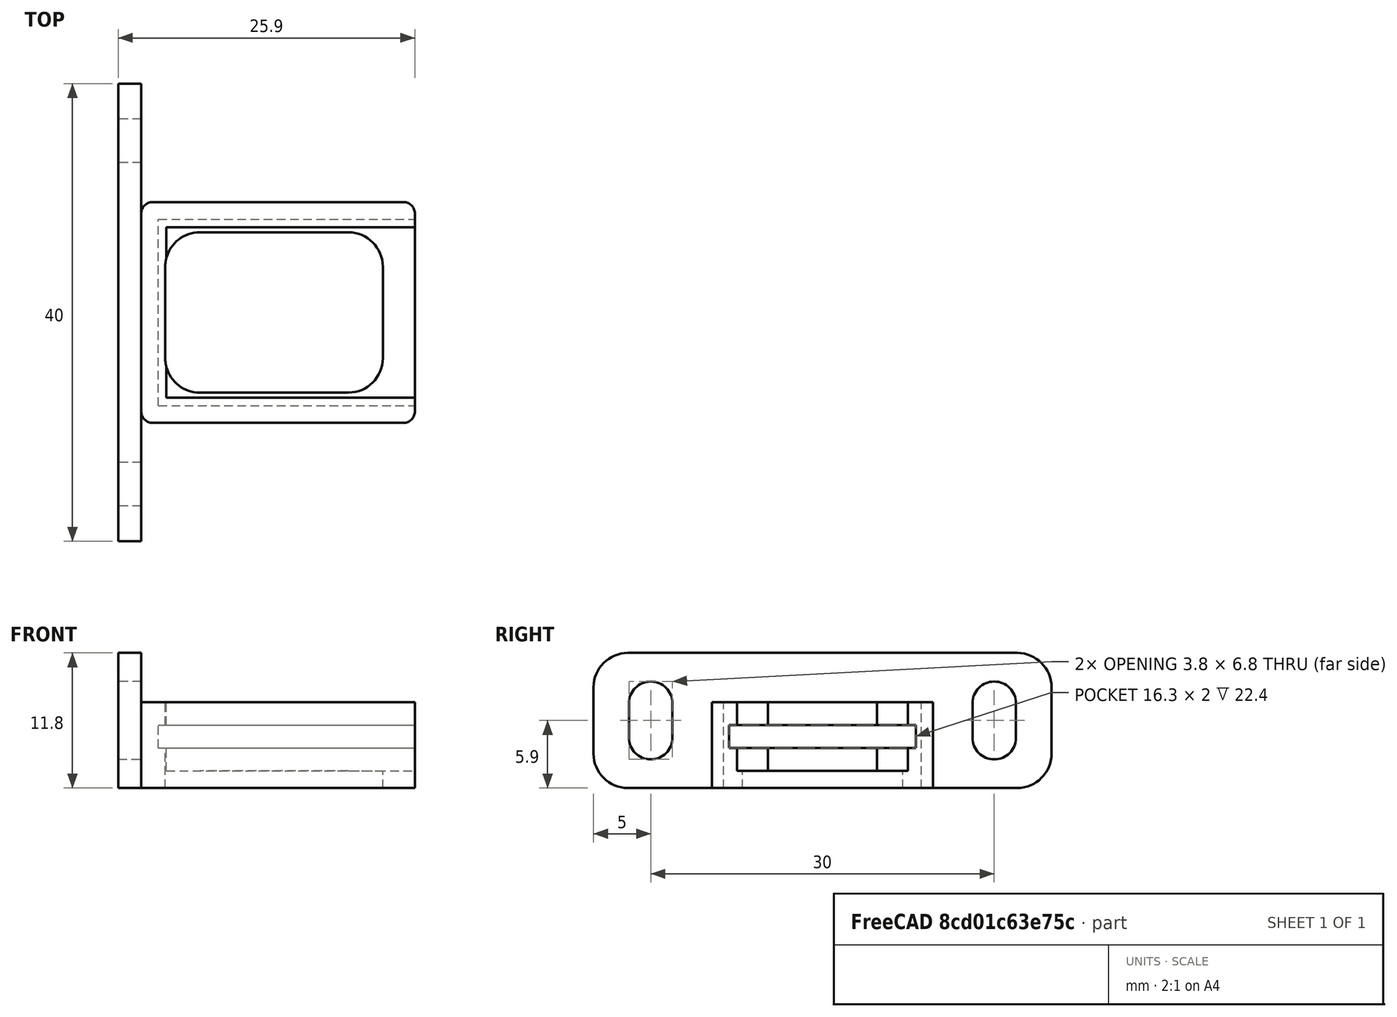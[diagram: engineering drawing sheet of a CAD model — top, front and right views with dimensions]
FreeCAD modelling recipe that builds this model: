
FCSTD DOCUMENT  (FreeCAD 0.21R33694 (Git))
Label: hlk-ld2410c
License: FreeArt
LicenseURL: http://artlibre.org/licence/lal
objects: Part::Box×4, Part::Fillet×2, Part::MultiFuse×2, Spreadsheet::Sheet×1, Part::Feature×1, Part::Cut×1, App::Part×1
note: 10 computed .brp shape members not serialized (recipe doc carries the construction recipe); baked Part::Feature solids carry a one-line shape summary decoded from their .brp

FEATURE [Spreadsheet::Sheet] Spreadsheet  label="p"
  cells = A1='pcb_x; B1(pcb_x)=22.4; A2='pcb_y; B2(pcb_y)=16.3; A3='pcb_z; B3(pcb_z)=2; A4='pcb_under; B4(pcb_under)=2; A5='side_wall; B5(side_wall)=1.5; A6='pcb_side_lane; B6(pcb_side_lane)=0.7; A7='bottom_wall; B7(bottom_wall)=1.5; A8='pcb_above; B8(pcb_above)=2; A9='bottom_hole_x; B9(bottom_hole_x)=19; A10='bottom_hole_y; B10(bottom_hole_y)=14
FEATURE [Part::Box] Box  label="external cube"
  AttacherType = Attacher::AttachEngine3D
  Height = 7.5
  Length = 23.9
  Width = 19.3
  expr: Height = <<p>>.bottom_wall + <<p>>.pcb_under + <<p>>.pcb_z + <<p>>.pcb_above
  expr: Length = <<p>>.pcb_x + <<p>>.side_wall
  expr: Width = <<p>>.pcb_y + 2 * <<p>>.side_wall
FEATURE [Part::Box] Box006  label="internal cube"
  AttacherType = Attacher::AttachEngine3D
  Height = 6
  Length = 22.5
  Placement = pos=(2.2,2.2,1.5) rot=(0,0,1;0rad)
  Width = 14.9
  expr: .Placement.Base.x = <<p>>.side_wall + <<p>>.pcb_side_lane
  expr: .Placement.Base.y = <<p>>.side_wall + <<p>>.pcb_side_lane
  expr: .Placement.Base.z = <<p>>.bottom_wall
  expr: Height = <<p>>.pcb_under + <<p>>.pcb_z + <<p>>.pcb_above
  expr: Length = <<p>>.pcb_x - 2 * <<p>>.pcb_side_lane + <<p>>.side_wall
  expr: Width = <<p>>.pcb_y - 2 * <<p>>.pcb_side_lane
FEATURE [Part::Box] Box007  label="pcb extract cube"
  AttacherType = Attacher::AttachEngine3D
  Height = 2
  Length = 22.4
  Placement = pos=(1.5,1.5,3.5) rot=(0,0,1;0rad)
  Width = 16.3
  expr: .Placement.Base.x = <<p>>.side_wall
  expr: .Placement.Base.y = <<p>>.side_wall
  expr: .Placement.Base.z = <<p>>.bottom_wall + <<p>>.pcb_under
  expr: Height = <<p>>.pcb_z
  expr: Length = <<p>>.pcb_x
  expr: Width = <<p>>.pcb_y
FEATURE [Part::Fillet] Fillet  label="external fillet"
  Base = -> Box
  Edges = 4 edges r=1: [Edge1,Edge3,Edge5,Edge7]
FEATURE [Part::Box] Box008  label="bottom hole"
  AttacherType = Attacher::AttachEngine3D
  Height = 10
  Length = 19
  Placement = pos=(2.1,2.65,0) rot=(0,0,1;0rad)
  Width = 14
  expr: .Placement.Base.x = (<<p>>.pcb_x + <<p>>.side_wall - <<p>>.pcb_side_lane - <<p>>.bottom_hole_x) / 2
  expr: .Placement.Base.y = (<<p>>.pcb_y + 2 * <<p>>.side_wall - <<p>>.bottom_hole_y) / 2
  expr: Length = <<p>>.bottom_hole_x
  expr: Width = <<p>>.bottom_hole_y
FEATURE [Part::Fillet] Fillet001  label="bottom hole fillet"
  Base = -> Box008
  Edges = 4 edges r=3: [Edge1,Edge3,Edge5,Edge7]
FEATURE [Part::MultiFuse] Fusion  label="extract fusion"
  Shapes = -> [Box006,Box007,Fillet001]
FEATURE [Part::Feature] Body003  label="attach plane y rotated dir001"
  Placement = pos=(0,-10.35,0) rot=(0,-1,0;1.5708rad)
  shape: bbox 2 x 40 x 11.8 mm, 20 faces (baked)
FEATURE [Part::MultiFuse] Fusion001  label="solid fusion"
  Shapes = -> [Fillet,Body003]
FEATURE [Part::Cut] Cut  label="body cut"
  Base = -> Fusion001
  Tool = -> Fusion
FEATURE [App::Part] Part  label="pcb box part"
  Group = -> [Box,Fillet,Fusion001,Fusion,Box007,Box006,Cut]
  Origin = -> Origin
